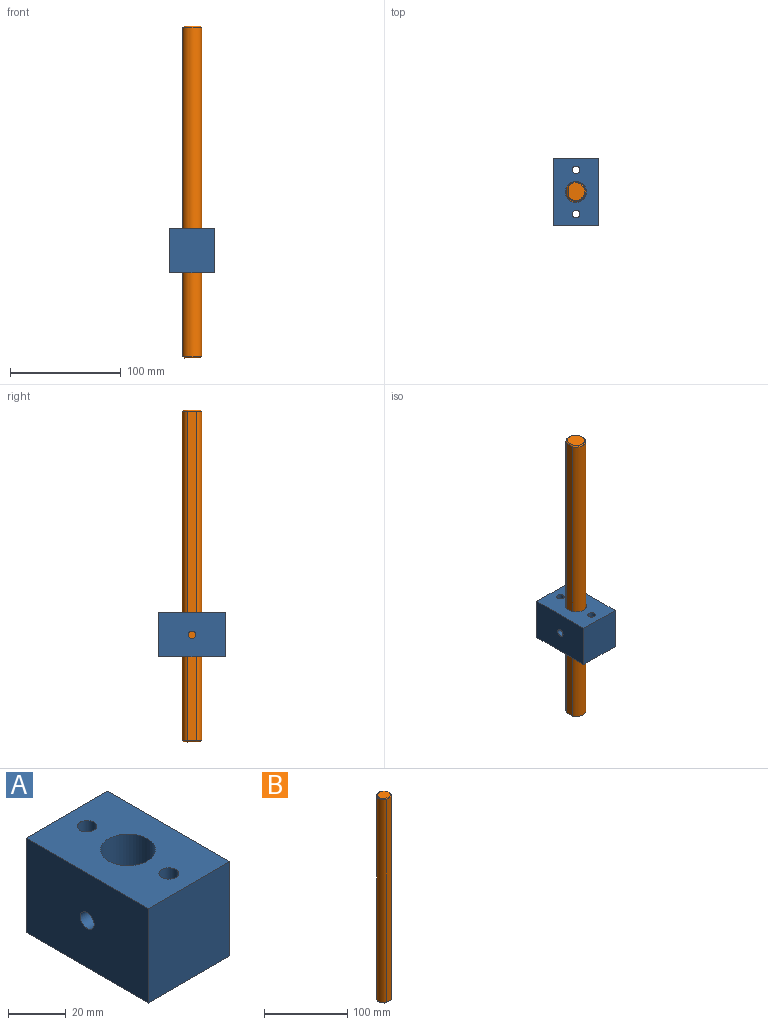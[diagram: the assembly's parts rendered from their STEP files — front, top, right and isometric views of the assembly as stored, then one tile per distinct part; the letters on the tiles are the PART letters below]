
ASSEMBLY  parts=2 mates=1
PART A: 10 faces, bbox 40x60x40 mm
  f0: plane 60x40mm, normal (-1,0,0), area 2363.7mm2, adj f1,f5,f7,f8,f9
  f1: plane 40x40mm, normal (0,-1,0), area 1600mm2, adj f0,f2,f7,f8
  f2: plane 60x40mm, normal (1,0,0), area 2400mm2, adj f1,f5,f7,f8
  f3: cylinder r=3.4mm len=40mm, axis (0,0,-1), area 854.5mm2, adj f7,f8
  f4: cylinder r=9.5mm len=40mm, axis (0,0,-1), area 2350.6mm2, adj f7,f8,f9
  f5: plane 40x40mm, normal (0,1,0), area 1600mm2, adj f0,f2,f7,f8
  f6: cylinder r=3.4mm len=40mm, axis (0,0,-1), area 854.5mm2, adj f7,f8
  f7: plane 60x40mm, normal (0,0,1), area 2043.8mm2, adj f0,f1,f2,f3,f4,f5,f6
  f8: plane 60x40mm, normal (0,0,-1), area 2043.8mm2, adj f0,f1,f2,f3,f4,f5,f6
  f9: cylinder r=3.4mm len=11.13mm, axis (-1,0,0), area 231mm2, adj f0,f4
PART B: 8 faces, bbox 18x17x300 mm
  f0: cylinder r=9mm len=298mm, axis (0,0,-1), area 14298.9mm2, adj f1,f4,f6
  f1: plane 298x8.25mm, normal (0,-1,0), area 2457.4mm2, adj f0,f5,f7
  f2: plane 16x15mm, normal (0,0,1), area 195.8mm2, adj f4,f5
  f3: plane 16x15mm, normal (0,0,-1), area 195.8mm2, adj f6,f7
  f4: cone r=8mm half-angle=45deg, axis (0,0,-1), area 63.7mm2, adj f0,f2,f5
  f5: plane 8.26x1.01mm, normal (0,-0.71,0.71), area 11.3mm2, adj f1,f2,f4
  f6: cone r=9mm half-angle=45deg, axis (0,0,1), area 63.7mm2, adj f0,f3,f7
  f7: plane 8.26x1.01mm, normal (0,-0.71,-0.71), area 11.3mm2, adj f1,f3,f6
PLACE A rot(axis=(-0.48,-0.84,-0.26),0deg) t=(-10.77,-19.43,-19.15)mm fixed
PLACE B rot(axis=(0,0,-1),90deg) t=(-10.97,-19.43,-96)mm
MATE slider B.f3 <-> A.f4  axis (0,0,-1) through (-10.77,-19.43,-96)mm
